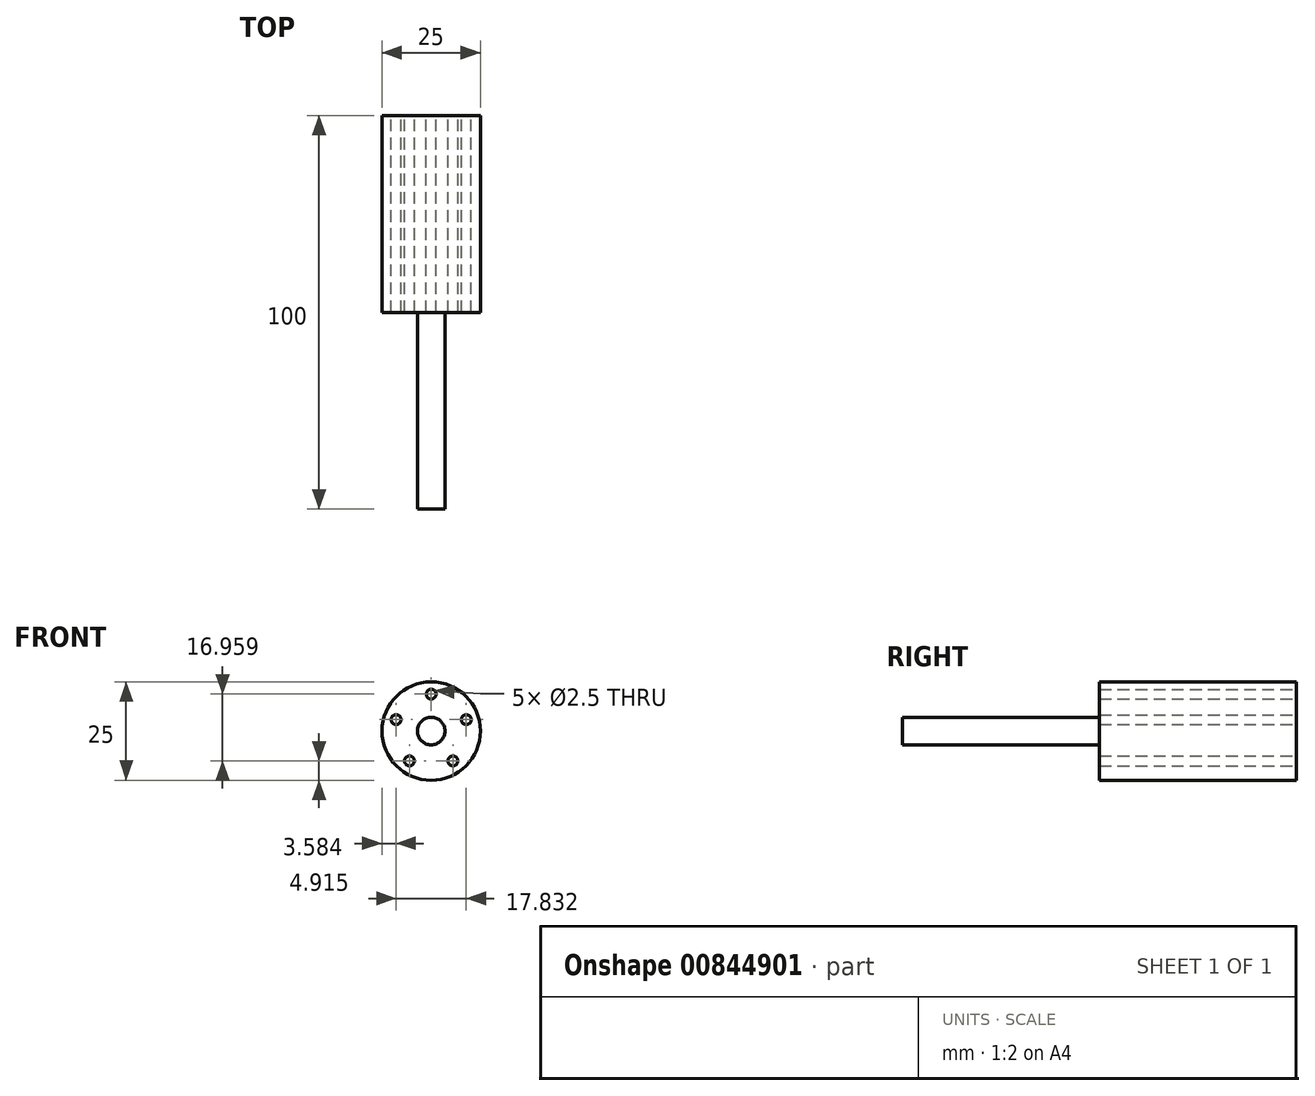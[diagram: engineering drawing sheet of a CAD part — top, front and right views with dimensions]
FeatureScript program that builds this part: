
annotation { "Feature Type Name" : "Feature", "Feature Type Description" : "" }
export const myFeature = defineFeature(function(context is Context, id is Id, definition is map)
    precondition{}
    {
        {
            var Q0;
            Q0=qCreatedBy(makeId("Front.planeOp"),FACE);
            var sketch = newSketch(context, id + "F0", { "sketchPlane" : qUnion([Q0])});
            skCircle(sketch, "E0", {"center": v(0, 0) * mm, "radius": 3.5 * mm});
            skSolve(sketch);
        }
        {
            var Q0;
            Q0 = qSketchRegion(id + "F0", true);
            extrude(context, id + "F1", {"entities" : qUnion([Q0]), "depth" : 100 * mm, "offsetDistance" : 25 * mm});
        }
        {
            var Q0;
            Q0=qCreatedBy(makeId("Front.planeOp"),FACE);
            var sketch = newSketch(context, id + "F2", { "sketchPlane" : qUnion([Q0])});
            skCircle(sketch, "E1", {"center": v(0, 0) * mm, "radius": 12.5 * mm});
            skLineSegment(sketch, "E2", {"start": v(0, 0) * mm, "end": v(0, 12.5) * mm, "construction": true});
            skLineSegment(sketch, "E3", {"start": v(0, 12.5) * mm, "end": v(0, 0) * mm, "construction": true});
            skLineSegment(sketch, "E4", {"start": v(0, 0) * mm, "end": v(-11.89, 3.86) * mm, "construction": true});
            skLineSegment(sketch, "E5", {"start": v(-11.89, 3.86) * mm, "end": v(0, 0) * mm, "construction": true});
            skLineSegment(sketch, "E6", {"start": v(0, 0) * mm, "end": v(-7.35, -10.11) * mm, "construction": true});
            skLineSegment(sketch, "E7", {"start": v(0, 0) * mm, "end": v(11.89, 3.86) * mm, "construction": true});
            skLineSegment(sketch, "E8", {"start": v(0, 0) * mm, "end": v(7.35, -10.11) * mm, "construction": true});
            skLineSegment(sketch, "E9", {"start": v(0, 6.25) * mm, "end": v(0, 12.5) * mm});
            skLineSegment(sketch, "E10", {"start": v(-5.94, 1.93) * mm, "end": v(-11.89, 3.86) * mm});
            skLineSegment(sketch, "E11", {"start": v(-3.67, -5.06) * mm, "end": v(-7.35, -10.11) * mm});
            skLineSegment(sketch, "E12", {"start": v(3.67, -5.06) * mm, "end": v(7.35, -10.11) * mm});
            skLineSegment(sketch, "E13", {"start": v(5.94, 1.93) * mm, "end": v(11.89, 3.86) * mm});
            skCircle(sketch, "E14", {"center": v(0, 9.38) * mm, "radius": 1.25 * mm});
            skCircle(sketch, "E15", {"center": v(-8.92, 2.9) * mm, "radius": 1.25 * mm});
            skCircle(sketch, "E16", {"center": v(-5.51, -7.58) * mm, "radius": 1.25 * mm});
            skCircle(sketch, "E17", {"center": v(5.51, -7.58) * mm, "radius": 1.25 * mm});
            skCircle(sketch, "E18", {"center": v(8.92, 2.9) * mm, "radius": 1.25 * mm});
            skSolve(sketch);
        }
        {
            var Q0;
            Q0=makeQuery(id+"F2.imprint","IMPRINT",FACE,{"disambiguationData":[TD([[makeQuery(id+"F2.imprint","IMPRINT",EDGE,{"derivedFrom":sQuery(id+"F2.wireOp",EDGE,"E1")}),1.0]])]});
            extrude(context, id + "F3", {"entities" : qUnion([Q0]), "operationType" : NewBodyOperationType.ADD, "depth" : 50 * mm, "offsetDistance" : 25 * mm});
        }
    });
